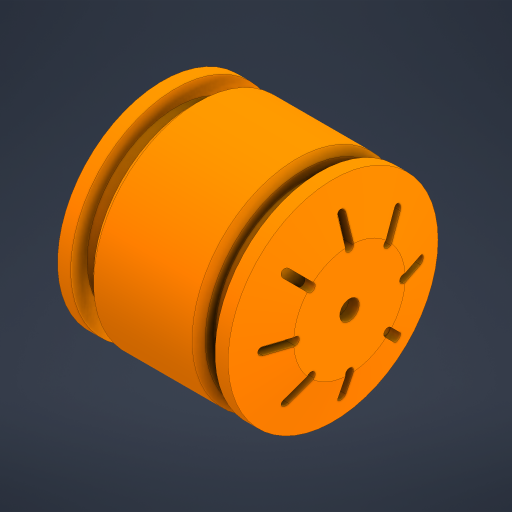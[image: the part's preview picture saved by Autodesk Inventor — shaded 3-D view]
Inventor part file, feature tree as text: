
AUTODESK INVENTOR PART (.ipt)
format: ipt  version: 2024 (Build 280153000, 153)  size: 506,880 bytes
history: native  units: mm
features: sketch x6, reference x6, other x5, extrude x4, revolve x2, projected_geometry x2, shell x1, chamfer x1, pattern_circular x1
ambient origin geometry x8: Origin, YZ Plane, XZ Plane, XY Plane, X Axis, Y Axis, Z Axis, Center Point
bodies: Body1 (feature_tree)
feature tree (28):
  other  "Твердое тело1"
  revolve  "Вращение1"
  revolve  "Вращение2"
  shell  "Оболочка1"  Thickness=32.0mm
  other  "РабПлоскость1"
  chamfer  "Фаска1"  Distance=27.0mm
  extrude  "Выдавливание6"  Depth=5.0mm
  extrude  "Выдавливание17"  Depth=34.0mm
  extrude  "Выдавливание18"  Depth=4.0mm
  extrude  "Выдавливание19"  TaperAngle=90.0deg  [1 undecoded]
  pattern_circular  "Круговой массив4"  [2 undecoded]
  sketch  "Эскиз1"
  sketch  "Эскиз2"
  sketch  "Эскиз9"
  sketch  "Эскиз21"
  projected_geometry  "Спроецированная петля5"
  sketch  "Эскиз22"
  reference  "Ссылка19"
  reference  "Ссылка20"
  reference  "Ссылка21"
  reference  "Ссылка22"
  reference  "Ссылка23"
  reference  "Ссылка24"
  sketch  "Эскиз23"
  projected_geometry  "Спроецированная петля6"
  parser-record x1  (decoder bookkeeping rows leaked as tree rows — omitted from the tree; the rows remain in map.json)
  other  "wheel_assembly.iam"
  other  "hex:1"
note: 3 required parameter values undecoded (feature->parameter linkage not recoverable at this tier; creation-order binding heuristic only, values carry confidence <= 0.55)
note: 1 file-system path scrubbed to <path> (originals preserved in map.json)
